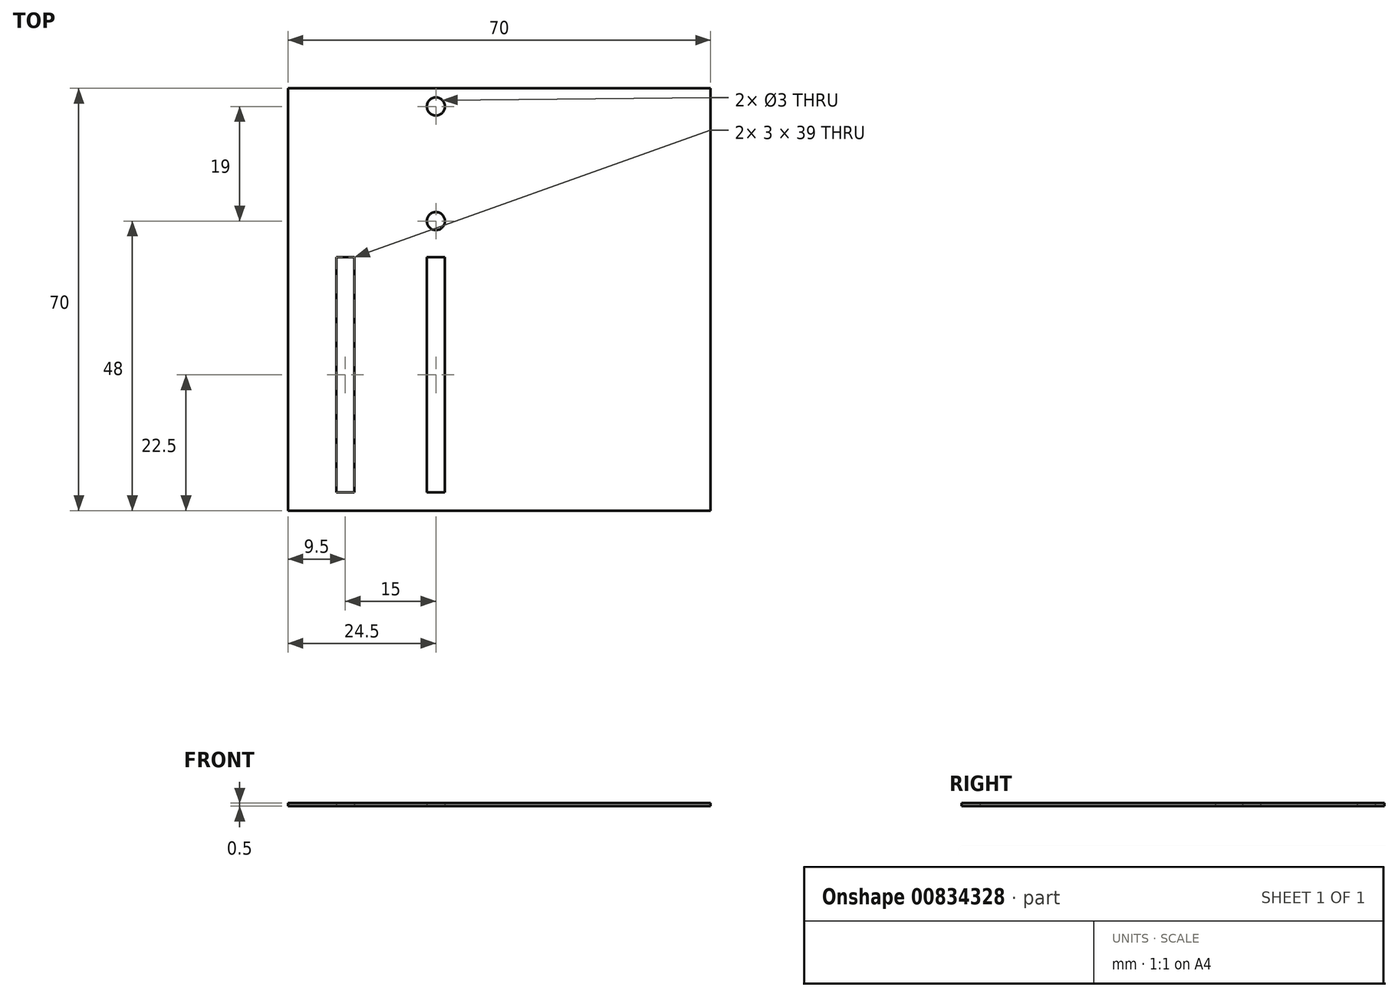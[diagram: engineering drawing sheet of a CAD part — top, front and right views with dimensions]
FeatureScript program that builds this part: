
annotation { "Feature Type Name" : "Feature", "Feature Type Description" : "" }
export const myFeature = defineFeature(function(context is Context, id is Id, definition is map)
    precondition{}
    {
        {
            var Q0;
            Q0=qCreatedBy(makeId("Top.planeOp"),FACE);
            var sketch = newSketch(context, id + "F0", { "sketchPlane" : qUnion([Q0])});
            skLineSegment(sketch, "E0.bottom", {"start": v(-70, -70) * mm, "end": v(0, -70) * mm});
            skLineSegment(sketch, "E0.top", {"start": v(-70, 0) * mm, "end": v(0, 0) * mm});
            skLineSegment(sketch, "E0.left", {"start": v(-70, -70) * mm, "end": v(-70, 0) * mm});
            skLineSegment(sketch, "E0.right", {"start": v(0, -70) * mm, "end": v(0, 0) * mm});
            skSolve(sketch);
        }
        {
            var Q0;
            Q0 = qSketchRegion(id + "F0", true);
            extrude(context, id + "F1", {"entities" : qUnion([Q0]), "depth" : 0.5 * mm, "offsetDistance" : 25 * mm});
        }
        {
            var Q0;
            Q0=qCreatedBy(makeId("Top.planeOp"),FACE);
            var sketch = newSketch(context, id + "F2", { "sketchPlane" : qUnion([Q0])});
            skLineSegment(sketch, "E1.bottom", {"start": v(-62, -28) * mm, "end": v(-59, -28) * mm});
            skLineSegment(sketch, "E1.top", {"start": v(-62, -67) * mm, "end": v(-59, -67) * mm});
            skLineSegment(sketch, "E1.left", {"start": v(-62, -28) * mm, "end": v(-62, -67) * mm});
            skLineSegment(sketch, "E1.right", {"start": v(-59, -28) * mm, "end": v(-59, -67) * mm});
            skLineSegment(sketch, "E2.left", {"start": v(-62, -28) * mm, "end": v(-62, -28) * mm});
            skLineSegment(sketch, "E2.right", {"start": v(-59, -28) * mm, "end": v(-59, -28) * mm});
            skLineSegment(sketch, "E3.bottom", {"start": v(-47, -28) * mm, "end": v(-44, -28) * mm});
            skLineSegment(sketch, "E3.top", {"start": v(-47, -67) * mm, "end": v(-44, -67) * mm});
            skLineSegment(sketch, "E3.left", {"start": v(-47, -28) * mm, "end": v(-47, -67) * mm});
            skLineSegment(sketch, "E3.right", {"start": v(-44, -28) * mm, "end": v(-44, -67) * mm});
            skLineSegment(sketch, "E4.left", {"start": v(-47, -28) * mm, "end": v(-47, -28) * mm});
            skLineSegment(sketch, "E4.right", {"start": v(-44, -28) * mm, "end": v(-44, -28) * mm});
            skCircle(sketch, "E5", {"center": v(-45.5, -3) * mm, "radius": 1.5 * mm});
            skCircle(sketch, "E6", {"center": v(-45.5, -22) * mm, "radius": 1.5 * mm});
            skPoint(sketch, "E7", {"position": v(-45.5, -28) * mm});
            skSolve(sketch);
        }
        {
            var Q0;
            Q0 = qSketchRegion(id + "F2", true);
            extrude(context, id + "F3", {"entities" : qUnion([Q0]), "operationType" : NewBodyOperationType.REMOVE, "endBound" : BoundingType.THROUGH_ALL, "depth" : 25 * mm, "offsetDistance" : 25 * mm});
        }
    });
